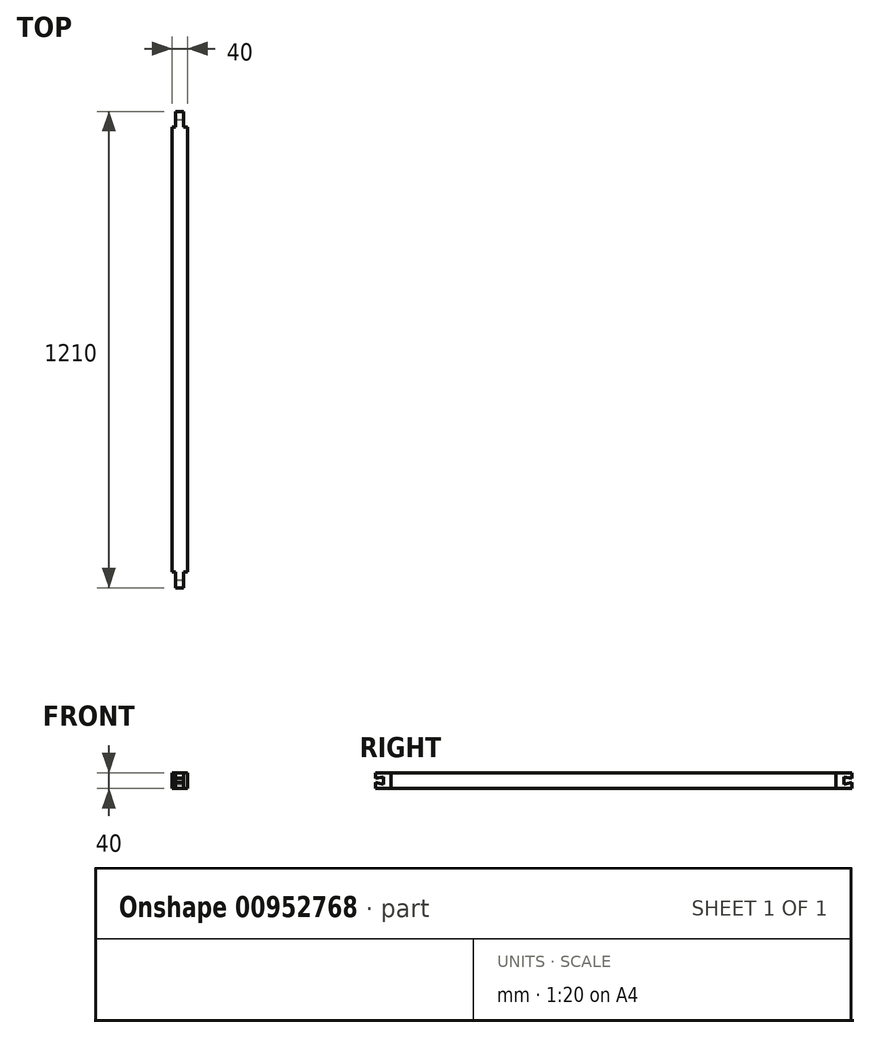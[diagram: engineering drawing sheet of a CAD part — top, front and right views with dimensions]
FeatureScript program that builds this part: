
annotation { "Feature Type Name" : "Feature", "Feature Type Description" : "" }
export const myFeature = defineFeature(function(context is Context, id is Id, definition is map)
    precondition{}
    {
        {
            var Q0;
            Q0=qCreatedBy(makeId("Front.planeOp"),FACE);
            var sketch = newSketch(context, id + "F0", { "sketchPlane" : qUnion([Q0])});
            skLineSegment(sketch, "E0.bottom", {"start": v(-19.88, 24.85) * mm, "end": v(20.12, 24.85) * mm});
            skLineSegment(sketch, "E0.top", {"start": v(-19.88, -15.15) * mm, "end": v(20.12, -15.15) * mm});
            skLineSegment(sketch, "E0.left", {"start": v(-19.88, 24.85) * mm, "end": v(-19.88, -15.15) * mm});
            skLineSegment(sketch, "E0.right", {"start": v(20.12, 24.85) * mm, "end": v(20.12, -15.15) * mm});
            skSolve(sketch);
        }
        {
            var Q0;
            Q0=makeQuery(id+"F0.imprint","IMPRINT",FACE,{"disambiguationData":[TD([[makeQuery(id+"F0.imprint","IMPRINT",EDGE,{"derivedFrom":sQuery(id+"F0.wireOp",EDGE,"E0.bottom")}),-1.0]])]});
            extrude(context, id + "F1", {"entities" : qUnion([Q0]), "depth" : 565 * mm, "offsetDistance" : 25 * mm});
        }
        {
            var Q0;
            Q0=makeQuery(id+"F1.opExtrude","CAP_FACE",FACE,{"disambiguationData":[OSD([sQuery(id+"F0.wireOp",EDGE,"E0.bottom"),sQuery(id+"F0.wireOp",EDGE,"E0.top"),sQuery(id+"F0.wireOp",EDGE,"E0.left"),sQuery(id+"F0.wireOp",EDGE,"E0.right")])],"isStart":false});
            var sketch = newSketch(context, id + "F2", { "sketchPlane" : qUnion([Q0])});
            skLineSegment(sketch, "E1.bottom", {"start": v(-9.88, 24.85) * mm, "end": v(10.12, 24.85) * mm});
            skLineSegment(sketch, "E1.top", {"start": v(-9.88, -15.15) * mm, "end": v(10.12, -15.15) * mm});
            skLineSegment(sketch, "E1.left", {"start": v(-9.88, 24.85) * mm, "end": v(-9.88, -15.15) * mm});
            skLineSegment(sketch, "E1.right", {"start": v(10.12, 24.85) * mm, "end": v(10.12, -15.15) * mm});
            skSolve(sketch);
        }
        {
            var Q0;
            Q0=makeQuery(id+"F2.imprint","IMPRINT",FACE,{"disambiguationData":[TD([[makeQuery(id+"F2.imprint","IMPRINT",EDGE,{"derivedFrom":sQuery(id+"F2.wireOp",EDGE,"E1.bottom")}),-1.0]])]});
            extrude(context, id + "F3", {"entities" : qUnion([Q0]), "operationType" : NewBodyOperationType.ADD, "depth" : 40 * mm, "offsetDistance" : 25 * mm});
        }
        {
            var Q0;
            Q0=makeQuery(id+"F3.opExtrude","SWEPT_FACE",FACE,{"disambiguationData":[OSD([sQuery(id+"F2.wireOp",EDGE,"E1.right")])]});
            var sketch = newSketch(context, id + "F4", { "sketchPlane" : qUnion([Q0])});
            skLineSegment(sketch, "E2", {"start": v(-605, 9.85) * mm, "end": v(-585, 14.85) * mm});
            skLineSegment(sketch, "E3", {"start": v(-585, 14.85) * mm, "end": v(-585, -5.15) * mm});
            skLineSegment(sketch, "E4", {"start": v(-585, -5.15) * mm, "end": v(-605, -0.15) * mm});
            skSolve(sketch);
        }
        {
            var Q0;
            {var subQ0=sQuery(id+"F4.wireOp",EDGE,"E2");Q0=makeQuery(id+"F4.imprint","IMPRINT",FACE,{"disambiguationData":[TD([[makeQuery(id+"F4.imprint","IMPRINT",EDGE,{"derivedFrom":subQ0}),-1.0]])]});}
            extrude(context, id + "F5", {"entities" : qUnion([Q0]), "operationType" : NewBodyOperationType.REMOVE, "oppositeDirection" : true, "depth" : 20 * mm, "offsetDistance" : 25 * mm});
        }
        {
            var Q0;
            Q0=makeQuery(id+"F1.opExtrude","SWEPT_BODY",BODY,{"disambiguationData":[OSD([sQuery(id+"F0.wireOp",EDGE,"E0.bottom"),sQuery(id+"F0.wireOp",EDGE,"E0.top"),sQuery(id+"F0.wireOp",EDGE,"E0.left"),sQuery(id+"F0.wireOp",EDGE,"E0.right")])]});
            var Q1;
            Q1=makeQuery(id+"F1.opExtrude","CAP_FACE",FACE,{"disambiguationData":[OSD([sQuery(id+"F0.wireOp",EDGE,"E0.bottom"),sQuery(id+"F0.wireOp",EDGE,"E0.top"),sQuery(id+"F0.wireOp",EDGE,"E0.left"),sQuery(id+"F0.wireOp",EDGE,"E0.right")])],"isStart":true});
            mirror(context, id + "F6", {"operationType" : NewBodyOperationType.ADD, "entities" : qUnion([Q0]), "mirrorPlane" : qUnion([Q1])});
        }
    });
